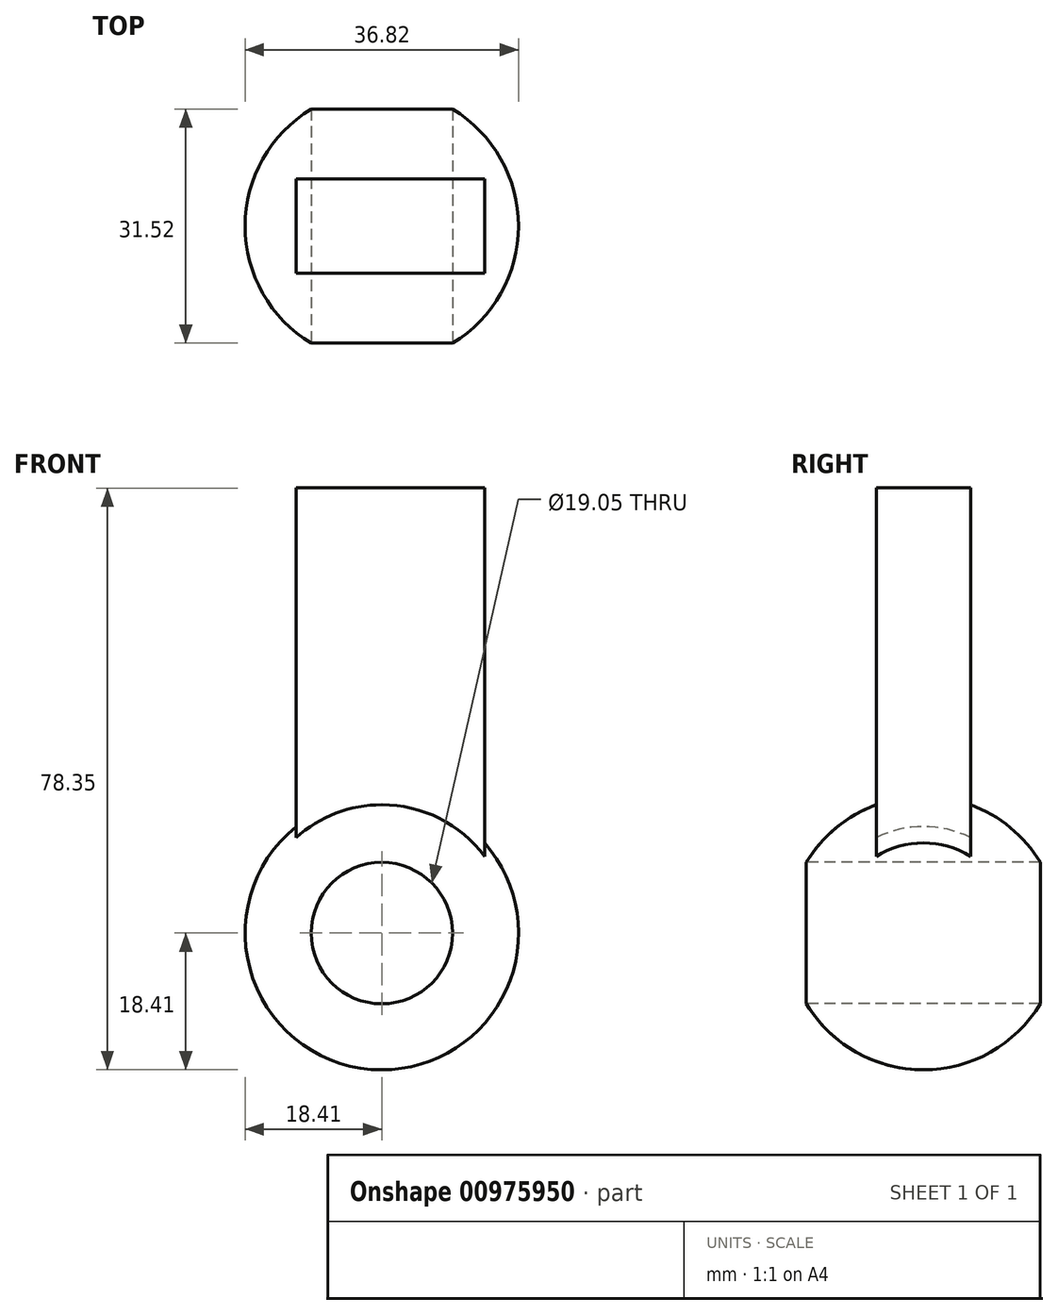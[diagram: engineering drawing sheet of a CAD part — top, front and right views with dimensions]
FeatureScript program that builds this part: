
annotation { "Feature Type Name" : "Feature", "Feature Type Description" : "" }
export const myFeature = defineFeature(function(context is Context, id is Id, definition is map)
    precondition{}
    {
        {
            var Q0;
            Q0=qCreatedBy(makeId("Right.planeOp"),FACE);
            var sketch = newSketch(context, id + "F0", { "sketchPlane" : qUnion([Q0])});
            skArc(sketch, "E0", {"start": v(0, -18.41) * mm, "mid": v(18.41, 0) * mm, "end": v(0, 18.41) * mm});
            skLineSegment(sketch, "E1", {"start": v(0, 0) * mm, "end": v(0, 18.41) * mm});
            skLineSegment(sketch, "E2", {"start": v(0, 18.41) * mm, "end": v(0, 0) * mm});
            skLineSegment(sketch, "E3", {"start": v(0, 0) * mm, "end": v(0, -18.41) * mm});
            skSolve(sketch);
        }
        {
            var Q0;
            Q0=makeQuery(id+"F0.imprint","IMPRINT",FACE,{"disambiguationData":[TD([[makeQuery(id+"F0.imprint","IMPRINT",EDGE,{"derivedFrom":sQuery(id+"F0.wireOp",EDGE,"E0")}),1.0]])]});
            var Q1;
            Q1=sQuery(id+"F0.wireOp",EDGE,"E3");
            revolve(context, id + "F1", {"surfaceOperationType" : NewSurfaceOperationType.NEW, "entities" : qUnion([Q0]), "axis" : qUnion([Q1]), "revolveType" : RevolveType.FULL});
        }
        {
            var Q0;
            Q0=qCreatedBy(makeId("Top.planeOp"),FACE);
            var sketch = newSketch(context, id + "F2", { "sketchPlane" : qUnion([Q0])});
            skLineSegment(sketch, "E4.bottom", {"start": v(-11.55, 6.35) * mm, "end": v(13.85, 6.35) * mm});
            skLineSegment(sketch, "E4.top", {"start": v(-11.55, -6.35) * mm, "end": v(13.85, -6.35) * mm});
            skLineSegment(sketch, "E4.left", {"start": v(-11.55, 6.35) * mm, "end": v(-11.55, -6.35) * mm});
            skLineSegment(sketch, "E4.right", {"start": v(13.85, 6.35) * mm, "end": v(13.85, -6.35) * mm});
            skLineSegment(sketch, "E5", {"start": v(0, 0) * mm, "end": v(0, -6.35) * mm});
            skSolve(sketch);
        }
        {
            var Q0;
            Q0 = qSketchRegion(id + "F2", true);
            extrude(context, id + "F3", {"entities" : qUnion([Q0]), "operationType" : NewBodyOperationType.ADD, "depth" : 59.94 * mm, "offsetDistance" : 25.4 * mm});
        }
        {
            var Q0;
            Q0=qCreatedBy(makeId("Front.planeOp"),FACE);
            var sketch = newSketch(context, id + "F4", { "sketchPlane" : qUnion([Q0])});
            skCircle(sketch, "E6", {"center": v(0, 0) * mm, "radius": 9.53 * mm});
            skSolve(sketch);
        }
        {
            var Q0;
            Q0 = qSketchRegion(id + "F4", true);
            extrude(context, id + "F5", {"entities" : qUnion([Q0]), "operationType" : NewBodyOperationType.REMOVE, "oppositeDirection" : true, "depth" : 76.2 * mm, "offsetDistance" : 25.4 * mm, "symmetric" : true});
        }
    });
